# Revit family: BE_77551_en_GB
name_source: partatom
category: Leuchten
units: mm (PartAtom-declared; Revit-internal decimal feet)

## family parameters
Basisbauteil = Fläche
Beim Laden mit Abzugskörper schneiden = Ja
Bemaßung runder Anschluss = Durchmesser verwenden
Gemeinsam genutzt = Nein
Lichtquelle = Nein
Raumberechnungspunkt = Ja
Teiletyp = Normal

## types (6) — shared parameters
AC/DC = AC/DC
Ambient_temperature = 25 °C
Beschreibung = Floodlight
CE_conformity = yes
Colour_rendering_index = CRI > 90
Custom_made_product = Nein
Description_custom_made_product = Here you can specify modifications of your custom-made product
ENEC = yes
Energy_efficiency_class = LED A++ - A
Fixing_distance = 48 x 160 mm
Fixing_hole = Ø 6,3 mm
Frequency = 0/50-60 Hz
Hersteller = BEGA
Lampe = LED 17.6 W
Load_Classification = Lighting
Logo = BEGA_Logo.png
Material_02 = BEGA_finishes_silver_matt
Material_03 = BEGA_finishes_white_matt
Material_06 = BEGA_finishes_stainless_steel_brushed
Material_09 = BEGA_glass_clear
Material_15 = BEGA_lighting_medium_matt
Material_17 = BEGA_reflector
Material_18 = BEGA_rubber_black
Product_data_sheet = https://cdn.bega.com
Protection_class = IP 65
Safety_class = I
Scheinlast = 0 VA
Service_life_criteria = L70B50 @ 25 °C = 200000 h
Typenbild = 77551.png
URL = https://www.bega.com
Update = 2022-05-19T04:00:15
Voltage = 240 V
Weight = 2.4 kg
zero-valued in all types: Vorgabe-Ansicht

## per-type parameters (varying)
| type | Bega_IES1 | Bega_IES2 | Colour_temperature | LED_module_designation | Lamp_luminous_flux | Luminaire_luminous_flux | M_A | M_G | M_W | Modell | Order_number |
| BEGA_77551_white_K3 | Ja | Nein | 3000 K | LED-0313/930 | 2780 lm | 2056 lm | Nein | Nein | Ja | 77551WK3 | 77551WK3 |
| BEGA_77551_white_K4 | Nein | Ja | 4000 K | LED-0313/940 | 2940 lm | 2174 lm | Nein | Nein | Ja | 77551WK4 | 77551WK4 |
| BEGA_77551_graphite_K4 | Nein | Ja | 4000 K | LED-0313/940 | 2940 lm | 2174 lm | Nein | Ja | Nein | 77551K4 | 77551K4 |
| BEGA_77551_silver_K3 | Ja | Nein | 3000 K | LED-0313/930 | 2780 lm | 2056 lm | Ja | Nein | Nein | 77551AK3 | 77551AK3 |
| BEGA_77551_silver_K4 | Nein | Ja | 4000 K | LED-0313/940 | 2940 lm | 2174 lm | Ja | Nein | Nein | 77551AK4 | 77551AK4 |
| BEGA_77551_graphite_K3 | Ja | Nein | 3000 K | LED-0313/930 | 2780 lm | 2056 lm | Nein | Ja | Nein | 77551K3 | 77551K3 |

## geometry (parser evidence)
native form markers: Sweep x31
no freeform markers — native parametric forms only
